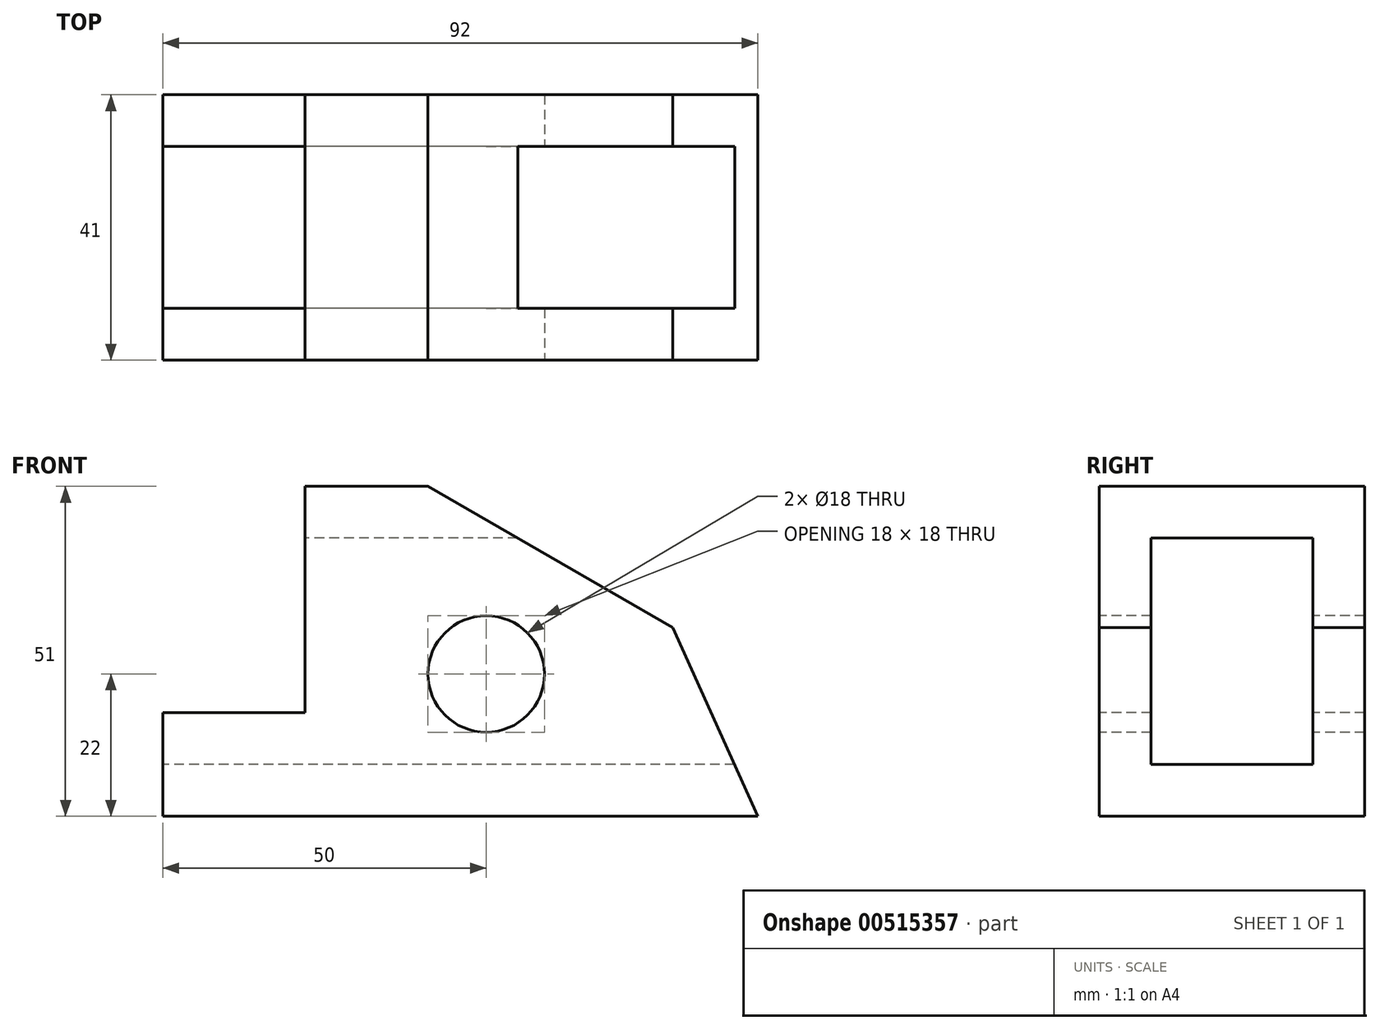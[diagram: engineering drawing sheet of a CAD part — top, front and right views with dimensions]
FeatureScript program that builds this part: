
annotation { "Feature Type Name" : "Feature", "Feature Type Description" : "" }
export const myFeature = defineFeature(function(context is Context, id is Id, definition is map)
    precondition{}
    {
        {
            var Q0;
            Q0=qCreatedBy(makeId("Front.planeOp"),FACE);
            var sketch = newSketch(context, id + "F0", { "sketchPlane" : qUnion([Q0])});
            skLineSegment(sketch, "E0.bottom", {"start": v(0, 0) * mm, "end": v(92, 0) * mm});
            skLineSegment(sketch, "E0.top", {"start": v(0, 51) * mm, "end": v(92, 51) * mm});
            skLineSegment(sketch, "E0.left", {"start": v(0, 0) * mm, "end": v(0, 51) * mm});
            skLineSegment(sketch, "E0.right", {"start": v(92, 0) * mm, "end": v(92, 51) * mm});
            skSolve(sketch);
        }
        {
            var Q0;
            Q0=makeQuery(id+"F0.imprint","IMPRINT",FACE,{"disambiguationData":[TD([[makeQuery(id+"F0.imprint","IMPRINT",EDGE,{"derivedFrom":sQuery(id+"F0.wireOp",EDGE,"E0.bottom")}),1.0]])]});
            extrude(context, id + "F1", {"entities" : qUnion([Q0]), "depth" : 41 * mm, "offsetDistance" : 25.4 * mm});
        }
        {
            var Q0;
            Q0=makeQuery(id+"F1.opExtrude","CAP_FACE",FACE,{"disambiguationData":[OSD([sQuery(id+"F0.wireOp",EDGE,"E0.bottom"),sQuery(id+"F0.wireOp",EDGE,"E0.top"),sQuery(id+"F0.wireOp",EDGE,"E0.left"),sQuery(id+"F0.wireOp",EDGE,"E0.right")])],"isStart":false});
            var sketch = newSketch(context, id + "F2", { "sketchPlane" : qUnion([Q0])});
            skLineSegment(sketch, "E1.bottom", {"start": v(0, 51) * mm, "end": v(22, 51) * mm});
            skLineSegment(sketch, "E1.top", {"start": v(0, 16) * mm, "end": v(22, 16) * mm});
            skLineSegment(sketch, "E1.left", {"start": v(0, 51) * mm, "end": v(0, 16) * mm});
            skLineSegment(sketch, "E1.right", {"start": v(22, 51) * mm, "end": v(22, 16) * mm});
            skSolve(sketch);
        }
        {
            var Q0;
            Q0=makeQuery(id+"F2.imprint","IMPRINT",FACE,{"disambiguationData":[TD([[makeQuery(id+"F2.imprint","IMPRINT",EDGE,{"derivedFrom":sQuery(id+"F2.wireOp",EDGE,"E1.bottom")}),-1.0]])]});
            extrude(context, id + "F3", {"entities" : qUnion([Q0]), "operationType" : NewBodyOperationType.REMOVE, "endBound" : BoundingType.THROUGH_ALL, "oppositeDirection" : true, "depth" : 25.4 * mm, "offsetDistance" : 25.4 * mm});
        }
        {
            var Q0;
            Q0=makeQuery(id+"F1.opExtrude","CAP_FACE",FACE,{"disambiguationData":[OSD([sQuery(id+"F0.wireOp",EDGE,"E0.bottom"),sQuery(id+"F0.wireOp",EDGE,"E0.top"),sQuery(id+"F0.wireOp",EDGE,"E0.left"),sQuery(id+"F0.wireOp",EDGE,"E0.right")])],"isStart":false});
            var sketch = newSketch(context, id + "F4", { "sketchPlane" : qUnion([Q0])});
            skLineSegment(sketch, "E2", {"start": v(22, 51) * mm, "end": v(41, 51) * mm});
            skLineSegment(sketch, "E3", {"start": v(41, 51) * mm, "end": v(78.82, 29.16) * mm});
            skLineSegment(sketch, "E4", {"start": v(92, 0) * mm, "end": v(78.82, 29.16) * mm});
            skLineSegment(sketch, "E5", {"start": v(41, 51) * mm, "end": v(92, 51) * mm});
            skLineSegment(sketch, "E6", {"start": v(92, 51) * mm, "end": v(92, 0) * mm});
            skSolve(sketch);
        }
        {
            var Q0;
            Q0 = qSketchRegion(id + "F4", true);
            extrude(context, id + "F5", {"entities" : qUnion([Q0]), "operationType" : NewBodyOperationType.REMOVE, "endBound" : BoundingType.THROUGH_ALL, "oppositeDirection" : true, "depth" : 25.4 * mm, "offsetDistance" : 25.4 * mm});
        }
        {
            var Q0;
            Q0=makeQuery(id+"F1.opExtrude","CAP_FACE",FACE,{"disambiguationData":[OSD([sQuery(id+"F0.wireOp",EDGE,"E0.bottom"),sQuery(id+"F0.wireOp",EDGE,"E0.top"),sQuery(id+"F0.wireOp",EDGE,"E0.left"),sQuery(id+"F0.wireOp",EDGE,"E0.right")])],"isStart":false});
            var sketch = newSketch(context, id + "F6", { "sketchPlane" : qUnion([Q0])});
            skCircle(sketch, "E7", {"center": v(50, 22) * mm, "radius": 9 * mm});
            skSolve(sketch);
        }
        {
            var Q0;
            Q0=makeQuery(id+"F6.imprint","IMPRINT",FACE,{"disambiguationData":[TD([[makeQuery(id+"F6.imprint","IMPRINT",EDGE,{"derivedFrom":sQuery(id+"F6.wireOp",EDGE,"E7")}),1.0]])]});
            extrude(context, id + "F7", {"entities" : qUnion([Q0]), "operationType" : NewBodyOperationType.REMOVE, "endBound" : BoundingType.THROUGH_ALL, "oppositeDirection" : true, "depth" : 25.4 * mm, "offsetDistance" : 25.4 * mm});
        }
        {
            var Q0;
            Q0=makeQuery(id+"F3.boolean.opBoolean","COPY",FACE,{"derivedFrom":makeQuery(id+"F3.opExtrude","SWEPT_FACE",FACE,{"disambiguationData":[OSD([sQuery(id+"F2.wireOp",EDGE,"E1.right")])]})});
            var sketch = newSketch(context, id + "F8", { "sketchPlane" : qUnion([Q0])});
            skLineSegment(sketch, "E8.bottom", {"start": v(8, 43) * mm, "end": v(33, 43) * mm});
            skLineSegment(sketch, "E8.top", {"start": v(8, 8) * mm, "end": v(33, 8) * mm});
            skLineSegment(sketch, "E8.left", {"start": v(8, 43) * mm, "end": v(8, 8) * mm});
            skLineSegment(sketch, "E8.right", {"start": v(33, 43) * mm, "end": v(33, 8) * mm});
            skSolve(sketch);
        }
        {
            var Q0;
            Q0 = qSketchRegion(id + "F8", true);
            extrude(context, id + "F9", {"entities" : qUnion([Q0]), "operationType" : NewBodyOperationType.REMOVE, "endBound" : BoundingType.THROUGH_ALL, "oppositeDirection" : true, "depth" : 25.4 * mm, "offsetDistance" : 25.4 * mm, "hasSecondDirection" : true, "secondDirectionOppositeDirection" : false, "secondDirectionDepth" : 25.4 * mm});
        }
    });
